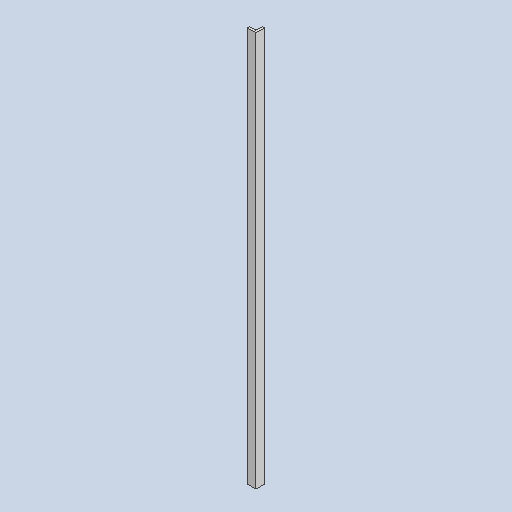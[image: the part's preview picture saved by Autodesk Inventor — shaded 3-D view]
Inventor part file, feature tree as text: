
AUTODESK INVENTOR PART (.ipt)
format: ipt  version: 2023 (Build 270158030, 158C)  size: 81,408 bytes
history: native  units: in
note: dims shown in document units (in); Inventor stores cm internally (conversion verified against a paired STEP export)
features: extrude x1, sketch x1
ambient origin geometry x8: Origin, YZ Plane, XZ Plane, XY Plane, X Axis, Y Axis, Z Axis, Center Point
bodies: Solid1 (feature_tree)
feature tree (2):
  extrude  "Extrusion1"  Depth=0.25in
  sketch  "Sketch1"  dims[d0=1.0in d1=0.25in d2=0.75in d3=0.75in d4=46.0in d5=0.0in]
